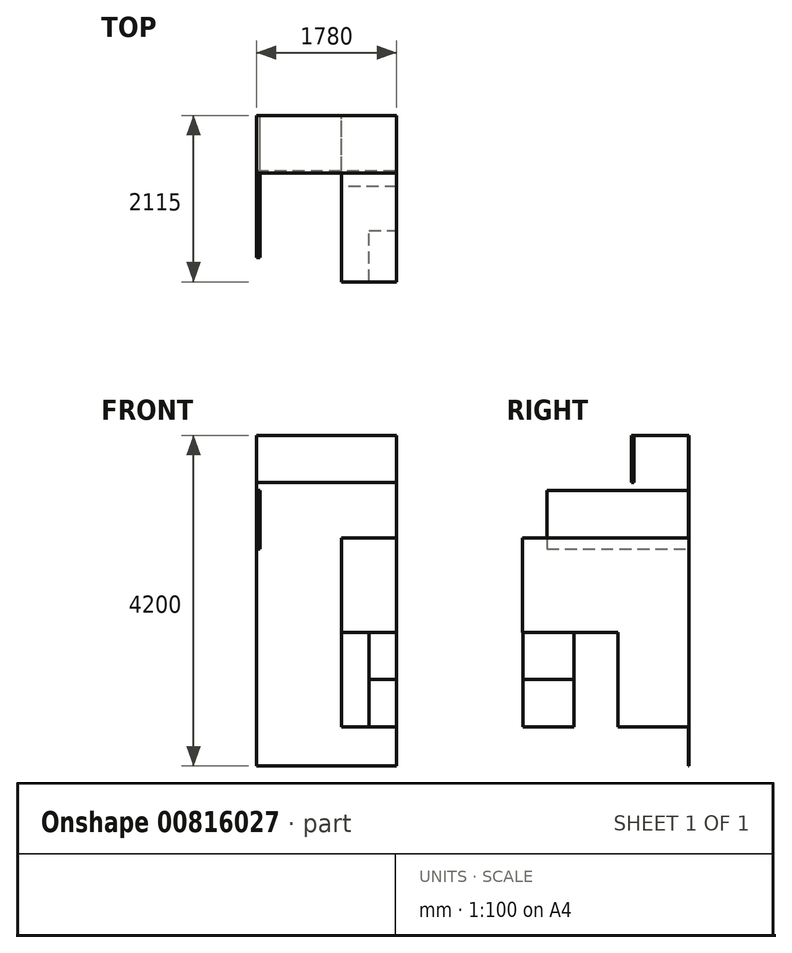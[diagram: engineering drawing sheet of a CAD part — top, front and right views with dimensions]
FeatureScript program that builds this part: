
annotation { "Feature Type Name" : "Feature", "Feature Type Description" : "" }
export const myFeature = defineFeature(function(context is Context, id is Id, definition is map)
    precondition{}
    {
        {
            var Q0;
            Q0=qCreatedBy(makeId("Front.planeOp"),FACE);
            var sketch = newSketch(context, id + "F0", { "sketchPlane" : qUnion([Q0])});
            skLineSegment(sketch, "E0.bottom", {"start": v(-890, 2100) * mm, "end": v(890, 2100) * mm});
            skLineSegment(sketch, "E0.top", {"start": v(-890, -2100) * mm, "end": v(890, -2100) * mm});
            skLineSegment(sketch, "E0.left", {"start": v(-890, 2100) * mm, "end": v(-890, -2100) * mm});
            skLineSegment(sketch, "E0.right", {"start": v(890, 2100) * mm, "end": v(890, -2100) * mm});
            skPoint(sketch, "E0.middle", {"position": v(0, 0) * mm});
            skSolve(sketch);
        }
        {
            var Q0;
            Q0=makeQuery(id+"F0.imprint","IMPRINT",FACE,{"disambiguationData":[TD([[makeQuery(id+"F0.imprint","IMPRINT",EDGE,{"derivedFrom":sQuery(id+"F0.wireOp",EDGE,"E0.bottom")}),-1.0]])]});
            extrude(context, id + "F1", {"entities" : qUnion([Q0]), "depth" : 5 * mm, "offsetDistance" : 25 * mm, "symmetric" : true});
        }
        {
            var Q0;
            Q0=makeQuery(id+"F1.opExtrude","CAP_FACE",FACE,{"disambiguationData":[OSD([sQuery(id+"F0.wireOp",EDGE,"E0.bottom"),sQuery(id+"F0.wireOp",EDGE,"E0.top"),sQuery(id+"F0.wireOp",EDGE,"E0.left"),sQuery(id+"F0.wireOp",EDGE,"E0.right")])],"isStart":false});
            var sketch = newSketch(context, id + "F2", { "sketchPlane" : qUnion([Q0])});
            skLineSegment(sketch, "E1.bottom", {"start": v(890, 2100) * mm, "end": v(-890, 2100) * mm});
            skLineSegment(sketch, "E1.top", {"start": v(890, 1500) * mm, "end": v(-890, 1500) * mm});
            skLineSegment(sketch, "E1.left", {"start": v(890, 2100) * mm, "end": v(890, 1500) * mm});
            skLineSegment(sketch, "E1.right", {"start": v(-890, 2100) * mm, "end": v(-890, 1500) * mm});
            skSolve(sketch);
        }
        {
            var Q0;
            Q0=makeQuery(id+"F2.imprint","IMPRINT",FACE,{"disambiguationData":[TD([[makeQuery(id+"F2.imprint","IMPRINT",EDGE,{"derivedFrom":sQuery(id+"F2.wireOp",EDGE,"E1.bottom")}),-1.0]])]});
            extrude(context, id + "F3", {"entities" : qUnion([Q0]), "operationType" : NewBodyOperationType.ADD, "depth" : 730 * mm, "offsetDistance" : 25 * mm});
        }
        {
            var Q0;
            Q0=makeQuery(id+"F3.opExtrude","SWEPT_FACE",FACE,{"disambiguationData":[OSD([sQuery(id+"F2.wireOp",EDGE,"E1.top")])]});
            var sketch = newSketch(context, id + "F4", { "sketchPlane" : qUnion([Q0])});
            skLineSegment(sketch, "E2.bottom", {"start": v(-890, 732.5) * mm, "end": v(890, 732.5) * mm});
            skLineSegment(sketch, "E2.top", {"start": v(-890, 697.5) * mm, "end": v(890, 697.5) * mm});
            skLineSegment(sketch, "E2.left", {"start": v(-890, 732.5) * mm, "end": v(-890, 697.5) * mm});
            skLineSegment(sketch, "E2.right", {"start": v(890, 732.5) * mm, "end": v(890, 697.5) * mm});
            skSolve(sketch);
        }
        {
            var Q0;
            {var subQ0=sQuery(id+"F4.wireOp",EDGE,"E2.top");Q0=makeQuery(id+"F4.imprint","IMPRINT",FACE,{"disambiguationData":[TD([[makeQuery(id+"F4.imprint","IMPRINT",EDGE,{"derivedFrom":subQ0}),-1.0]])]});}
            extrude(context, id + "F5", {"entities" : qUnion([Q0]), "operationType" : NewBodyOperationType.REMOVE, "oppositeDirection" : true, "depth" : 599 * mm, "offsetDistance" : 25 * mm});
        }
        {
            var Q0;
            Q0=makeQuery(id+"F5.boolean.opBoolean","MERGE",FACE,{"derivedFrom":[makeQuery(id+"F1.opExtrude","CAP_FACE",FACE,{"disambiguationData":[OSD([sQuery(id+"F0.wireOp",EDGE,"E0.bottom"),sQuery(id+"F0.wireOp",EDGE,"E0.top"),sQuery(id+"F0.wireOp",EDGE,"E0.left"),sQuery(id+"F0.wireOp",EDGE,"E0.right")])],"isStart":false}),makeQuery(id+"F5.opExtrude","SWEPT_FACE",FACE,{"disambiguationData":[OSD([sQuery(id+"F2.wireOp",EDGE,"E1.top")])]})]});
            var sketch = newSketch(context, id + "F6", { "sketchPlane" : qUnion([Q0])});
            skLineSegment(sketch, "E3", {"start": v(890, 2099) * mm, "end": v(890, 799) * mm});
            skLineSegment(sketch, "E4.bottom", {"start": v(890, 799) * mm, "end": v(190, 799) * mm});
            skLineSegment(sketch, "E4.top", {"start": v(890, 199) * mm, "end": v(190, 199) * mm});
            skLineSegment(sketch, "E4.left", {"start": v(890, 799) * mm, "end": v(890, 199) * mm});
            skLineSegment(sketch, "E4.right", {"start": v(190, 799) * mm, "end": v(190, 199) * mm});
            skLineSegment(sketch, "E5", {"start": v(-890, 2099) * mm, "end": v(-890, 1399) * mm});
            skLineSegment(sketch, "E6.bottom", {"start": v(-890, 1399) * mm, "end": v(-845, 1399) * mm});
            skLineSegment(sketch, "E6.top", {"start": v(-890, 659) * mm, "end": v(-845, 659) * mm});
            skLineSegment(sketch, "E6.left", {"start": v(-890, 1399) * mm, "end": v(-890, 659) * mm});
            skLineSegment(sketch, "E6.right", {"start": v(-845, 1399) * mm, "end": v(-845, 659) * mm});
            skSolve(sketch);
        }
        {
            var Q0;
            Q0=makeQuery(id+"F6.imprint","IMPRINT",FACE,{"disambiguationData":[TD([[makeQuery(id+"F6.imprint","IMPRINT",EDGE,{"derivedFrom":sQuery(id+"F6.wireOp",EDGE,"E4.bottom")}),1.0]])]});
            extrude(context, id + "F7", {"entities" : qUnion([Q0]), "operationType" : NewBodyOperationType.ADD, "depth" : 2110 * mm, "offsetDistance" : 25 * mm});
        }
        {
            var Q0;
            Q0=makeQuery(id+"F5.boolean.opBoolean","MERGE",FACE,{"derivedFrom":[makeQuery(id+"F1.opExtrude","CAP_FACE",FACE,{"disambiguationData":[OSD([sQuery(id+"F0.wireOp",EDGE,"E0.bottom"),sQuery(id+"F0.wireOp",EDGE,"E0.top"),sQuery(id+"F0.wireOp",EDGE,"E0.left"),sQuery(id+"F0.wireOp",EDGE,"E0.right")])],"isStart":false}),makeQuery(id+"F5.opExtrude","SWEPT_FACE",FACE,{"disambiguationData":[OSD([sQuery(id+"F2.wireOp",EDGE,"E1.top")])]})]});
            var sketch = newSketch(context, id + "F8", { "sketchPlane" : qUnion([Q0])});
            skLineSegment(sketch, "E7.bottom", {"start": v(890, 199) * mm, "end": v(190, 199) * mm});
            skLineSegment(sketch, "E7.top", {"start": v(890, -401) * mm, "end": v(190, -401) * mm});
            skLineSegment(sketch, "E7.left", {"start": v(890, 199) * mm, "end": v(890, -401) * mm});
            skLineSegment(sketch, "E7.right", {"start": v(190, 199) * mm, "end": v(190, -401) * mm});
            skLineSegment(sketch, "E8.top", {"start": v(890, -1001) * mm, "end": v(190, -1001) * mm});
            skLineSegment(sketch, "E8.left", {"start": v(890, -401) * mm, "end": v(890, -1001) * mm});
            skLineSegment(sketch, "E8.right", {"start": v(190, -401) * mm, "end": v(190, -1001) * mm});
            skLineSegment(sketch, "E9.top", {"start": v(890, -1601) * mm, "end": v(190, -1601) * mm});
            skLineSegment(sketch, "E9.left", {"start": v(890, -1001) * mm, "end": v(890, -1601) * mm});
            skLineSegment(sketch, "E9.right", {"start": v(190, -1001) * mm, "end": v(190, -1601) * mm});
            skSolve(sketch);
        }
        {
            var Q0;
            Q0=makeQuery(id+"F8.imprint","IMPRINT",FACE,{"disambiguationData":[TD([[makeQuery(id+"F8.imprint","IMPRINT",EDGE,{"derivedFrom":sQuery(id+"F8.wireOp",EDGE,"E7.bottom")}),1.0]])]});
            extrude(context, id + "F9", {"entities" : qUnion([Q0]), "operationType" : NewBodyOperationType.ADD, "depth" : 2110 * mm, "offsetDistance" : 25 * mm});
        }
        {
            var Q0;
            Q0=makeQuery(id+"F5.boolean.opBoolean","MERGE",FACE,{"derivedFrom":[makeQuery(id+"F1.opExtrude","CAP_FACE",FACE,{"disambiguationData":[OSD([sQuery(id+"F0.wireOp",EDGE,"E0.bottom"),sQuery(id+"F0.wireOp",EDGE,"E0.top"),sQuery(id+"F0.wireOp",EDGE,"E0.left"),sQuery(id+"F0.wireOp",EDGE,"E0.right")])],"isStart":false}),makeQuery(id+"F5.opExtrude","SWEPT_FACE",FACE,{"disambiguationData":[OSD([sQuery(id+"F2.wireOp",EDGE,"E1.top")])]})]});
            var sketch = newSketch(context, id + "F10", { "sketchPlane" : qUnion([Q0])});
            skLineSegment(sketch, "E10.bottom", {"start": v(890, -401) * mm, "end": v(190, -401) * mm});
            skLineSegment(sketch, "E10.top", {"start": v(890, -1001) * mm, "end": v(190, -1001) * mm});
            skLineSegment(sketch, "E10.left", {"start": v(890, -401) * mm, "end": v(890, -1001) * mm});
            skLineSegment(sketch, "E10.right", {"start": v(190, -401) * mm, "end": v(190, -1001) * mm});
            skSolve(sketch);
        }
        {
            var Q0;
            Q0=makeQuery(id+"F10.imprint","IMPRINT",FACE,{"disambiguationData":[TD([[makeQuery(id+"F10.imprint","IMPRINT",EDGE,{"derivedFrom":sQuery(id+"F10.wireOp",EDGE,"E10.bottom")}),1.0]])]});
            extrude(context, id + "F11", {"entities" : qUnion([Q0]), "operationType" : NewBodyOperationType.ADD, "depth" : 900 * mm, "offsetDistance" : 25 * mm});
        }
        {
            var Q0;
            Q0=makeQuery(id+"F5.boolean.opBoolean","MERGE",FACE,{"derivedFrom":[makeQuery(id+"F1.opExtrude","CAP_FACE",FACE,{"disambiguationData":[OSD([sQuery(id+"F0.wireOp",EDGE,"E0.bottom"),sQuery(id+"F0.wireOp",EDGE,"E0.top"),sQuery(id+"F0.wireOp",EDGE,"E0.left"),sQuery(id+"F0.wireOp",EDGE,"E0.right")])],"isStart":false}),makeQuery(id+"F5.opExtrude","SWEPT_FACE",FACE,{"disambiguationData":[OSD([sQuery(id+"F2.wireOp",EDGE,"E1.top")])]})]});
            var sketch = newSketch(context, id + "F12", { "sketchPlane" : qUnion([Q0])});
            skLineSegment(sketch, "E11.bottom", {"start": v(890, -1001) * mm, "end": v(190, -1001) * mm});
            skLineSegment(sketch, "E11.top", {"start": v(890, -1601) * mm, "end": v(190, -1601) * mm});
            skLineSegment(sketch, "E11.left", {"start": v(890, -1001) * mm, "end": v(890, -1601) * mm});
            skLineSegment(sketch, "E11.right", {"start": v(190, -1001) * mm, "end": v(190, -1601) * mm});
            skSolve(sketch);
        }
        {
            var Q0;
            Q0=makeQuery(id+"F12.imprint","IMPRINT",FACE,{"disambiguationData":[TD([[makeQuery(id+"F12.imprint","IMPRINT",EDGE,{"derivedFrom":sQuery(id+"F12.wireOp",EDGE,"E11.bottom")}),1.0]])]});
            extrude(context, id + "F13", {"entities" : qUnion([Q0]), "operationType" : NewBodyOperationType.ADD, "depth" : 900 * mm, "offsetDistance" : 25 * mm});
        }
        {
            var Q0;
            Q0=makeQuery(id+"F13.boolean.opBoolean","MERGE",FACE,{"derivedFrom":[makeQuery(id+"F11.boolean.opBoolean","MERGE",FACE,{"derivedFrom":[makeQuery(id+"F9.boolean.opBoolean","MERGE",FACE,{"derivedFrom":[makeQuery(id+"F7.boolean.opBoolean","MERGE",FACE,{"derivedFrom":[makeQuery(id+"F3.boolean.opBoolean","MERGE",FACE,{"derivedFrom":[makeQuery(id+"F1.opExtrude","SWEPT_FACE",FACE,{"disambiguationData":[OSD([sQuery(id+"F0.wireOp",EDGE,"E0.right")])]}),makeQuery(id+"F3.opExtrude","SWEPT_FACE",FACE,{"disambiguationData":[OSD([sQuery(id+"F2.wireOp",EDGE,"E1.left")])]})]}),makeQuery(id+"F7.opExtrude","SWEPT_FACE",FACE,{"disambiguationData":[OSD([sQuery(id+"F6.wireOp",EDGE,"E4.left")])]})]}),makeQuery(id+"F9.opExtrude","SWEPT_FACE",FACE,{"disambiguationData":[OSD([sQuery(id+"F8.wireOp",EDGE,"E7.left")])]})]}),makeQuery(id+"F11.opExtrude","SWEPT_FACE",FACE,{"disambiguationData":[OSD([sQuery(id+"F10.wireOp",EDGE,"E10.left")])]})]}),makeQuery(id+"F13.opExtrude","SWEPT_FACE",FACE,{"disambiguationData":[OSD([sQuery(id+"F12.wireOp",EDGE,"E11.left")])]})]});
            var sketch = newSketch(context, id + "F14", { "sketchPlane" : qUnion([Q0])});
            skLineSegment(sketch, "E12", {"start": v(2.5, -401) * mm, "end": v(-1457.5, -401) * mm});
            skLineSegment(sketch, "E13.bottom", {"start": v(-1457.5, -401) * mm, "end": v(-2107.5, -401) * mm});
            skLineSegment(sketch, "E13.top", {"start": v(-1457.5, -1001) * mm, "end": v(-2107.5, -1001) * mm});
            skLineSegment(sketch, "E13.left", {"start": v(-1457.5, -401) * mm, "end": v(-1457.5, -1001) * mm});
            skLineSegment(sketch, "E13.right", {"start": v(-2107.5, -401) * mm, "end": v(-2107.5, -1001) * mm});
            skSolve(sketch);
        }
        {
            var Q0;
            Q0=makeQuery(id+"F14.imprint","IMPRINT",FACE,{"disambiguationData":[TD([[makeQuery(id+"F14.imprint","IMPRINT",EDGE,{"derivedFrom":sQuery(id+"F14.wireOp",EDGE,"E13.top")}),-1.0]])]});
            extrude(context, id + "F15", {"entities" : qUnion([Q0]), "oppositeDirection" : true, "depth" : 350 * mm, "offsetDistance" : 25 * mm});
        }
        {
            var Q0;
            Q0=makeQuery(id+"F15.opExtrude","CAP_FACE",FACE,{"disambiguationData":[OSD([sQuery(id+"F14.wireOp",EDGE,"E13.bottom"),sQuery(id+"F14.wireOp",EDGE,"E13.top"),sQuery(id+"F14.wireOp",EDGE,"E13.left"),sQuery(id+"F14.wireOp",EDGE,"E13.right")])],"isStart":true});
            var sketch = newSketch(context, id + "F16", { "sketchPlane" : qUnion([Q0])});
            skLineSegment(sketch, "E14.bottom", {"start": v(-2107.5, -1001) * mm, "end": v(-1457.5, -1001) * mm});
            skLineSegment(sketch, "E14.top", {"start": v(-2107.5, -1601) * mm, "end": v(-1457.5, -1601) * mm});
            skLineSegment(sketch, "E14.left", {"start": v(-2107.5, -1001) * mm, "end": v(-2107.5, -1601) * mm});
            skLineSegment(sketch, "E14.right", {"start": v(-1457.5, -1001) * mm, "end": v(-1457.5, -1601) * mm});
            skSolve(sketch);
        }
        {
            var Q0;
            Q0=makeQuery(id+"F16.imprint","IMPRINT",FACE,{"disambiguationData":[TD([[makeQuery(id+"F16.imprint","IMPRINT",EDGE,{"derivedFrom":sQuery(id+"F16.wireOp",EDGE,"E14.bottom")}),1.0]])]});
            extrude(context, id + "F17", {"entities" : qUnion([Q0]), "oppositeDirection" : true, "depth" : 350 * mm, "offsetDistance" : 25 * mm});
        }
        {
            var Q0;
            Q0=makeQuery(id+"F6.imprint","IMPRINT",FACE,{"disambiguationData":[TD([[makeQuery(id+"F6.imprint","IMPRINT",EDGE,{"derivedFrom":sQuery(id+"F6.wireOp",EDGE,"E6.bottom")}),-1.0]])]});
            extrude(context, id + "F18", {"entities" : qUnion([Q0]), "operationType" : NewBodyOperationType.ADD, "depth" : 1800 * mm, "offsetDistance" : 25 * mm});
        }
    });
